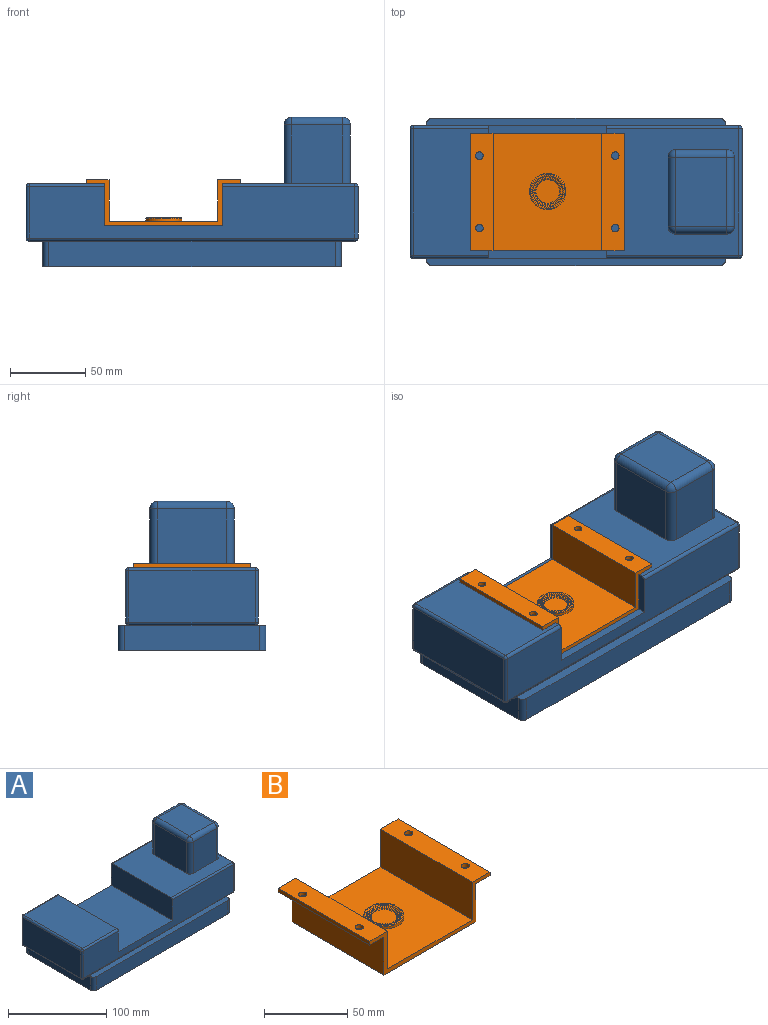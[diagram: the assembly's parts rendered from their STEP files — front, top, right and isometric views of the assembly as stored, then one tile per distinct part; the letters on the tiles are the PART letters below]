
ASSEMBLY  parts=2 mates=1
PART A: 61 faces, bbox 220x98x99 mm
  f0: plane 198x7mm, normal (0,0,1), area 1379.1mm2, adj f2,f3,f4,f7,f8,f37
  f1: plane 198x7mm, normal (0,0,1), area 1379.1mm2, adj f2,f4,f5,f9,f10,f29
  f2: plane 90x17mm, normal (-1,0,0), area 1530mm2, adj f0,f1,f6,f7,f10,f11
  f3: plane 190x17mm, normal (0,-1,0), area 3230mm2, adj f0,f6,f7,f8
  f4: plane 90x17mm, normal (1,0,0), area 1530mm2, adj f0,f1,f6,f8,f9,f18
  f5: plane 190x17mm, normal (0,1,0), area 3230mm2, adj f1,f6,f9,f10
  f6: plane 198x98mm, normal (0,0,-1), area 19390.3mm2, adj f2,f3,f4,f5,f7,f8,f9,f10
  f7: cylinder r=4mm len=17mm, axis (0,0,-1), area 106.8mm2, adj f0,f2,f3,f6
  f8: cylinder r=4mm len=17mm, axis (0,0,1), area 106.8mm2, adj f0,f3,f4,f6
  f9: cylinder r=4mm len=17mm, axis (0,0,-1), area 106.8mm2, adj f1,f4,f5,f6
  f10: cylinder r=4mm len=17mm, axis (0,0,1), area 106.8mm2, adj f1,f2,f5,f6
  f11: plane 84x9mm, normal (0,0,-1), area 756mm2, adj f2,f29,f30,f37
  f12: plane 88x84mm, normal (0,0,1), area 4949.5mm2, adj f19,f34,f40,f43,f44,f45,f46,f47
  f13: plane 216x34mm, normal (0,-1,0), area 5316mm2, adj f19,f20,f21,f26,f31,f37,f41,f43
  f14: plane 216x34mm, normal (0,1,0), area 5316mm2, adj f19,f20,f21,f22,f24,f29,f34,f35
  f15: plane 84x34mm, normal (-1,0,0), area 2856mm2, adj f24,f25,f30,f31
  f16: plane 84x34mm, normal (1,0,0), area 2856mm2, adj f35,f36,f40,f41
  f17: plane 84x50mm, normal (0,0,1), area 4200mm2, adj f20,f22,f25,f26
  f18: plane 84x9mm, normal (0,0,-1), area 756mm2, adj f4,f29,f36,f37
  f19: plane 88x28mm, normal (-1,0,0), area 2462.3mm2, adj f12,f13,f14,f21,f34,f43
  f20: plane 88x28mm, normal (1,0,0), area 2462.3mm2, adj f13,f14,f17,f21,f22,f26
  f21: plane 88x78mm, normal (0,0,1), area 6864mm2, adj f13,f14,f19,f20
  f22: cylinder r=2mm len=50mm, axis (1,0,0), area 157.1mm2, adj f14,f17,f20,f23
  f23: sphere r=2mm, area 6.3mm2, adj f22,f24,f25
  f24: cylinder r=2mm len=34mm, axis (0,0,1), area 106.8mm2, adj f14,f15,f23,f27
  f25: cylinder r=2mm len=84mm, axis (0,1,0), area 263.9mm2, adj f15,f17,f23,f28
  f26: cylinder r=2mm len=50mm, axis (-1,0,0), area 157.1mm2, adj f13,f17,f20,f28
  f27: sphere r=2mm, area 6.3mm2, adj f24,f29,f30
  f28: sphere r=2mm, area 6.3mm2, adj f25,f26,f31
  f29: cylinder r=2mm len=216mm, axis (-1,0,0), area 678.6mm2, adj f1,f11,f14,f18,f27,f32
  f30: cylinder r=2mm len=84mm, axis (0,-1,0), area 263.9mm2, adj f11,f15,f27,f33
  f31: cylinder r=2mm len=34mm, axis (0,0,-1), area 106.8mm2, adj f13,f15,f28,f33
  f32: sphere r=2mm, area 6.3mm2, adj f29,f35,f36
  f33: sphere r=2mm, area 6.3mm2, adj f30,f31,f37
  f34: cylinder r=2mm len=88mm, axis (1,0,0), area 276.5mm2, adj f12,f14,f19,f38
  f35: cylinder r=2mm len=34mm, axis (0,0,-1), area 106.8mm2, adj f14,f16,f32,f38
  f36: cylinder r=2mm len=84mm, axis (0,1,0), area 263.9mm2, adj f16,f18,f32,f39
  f37: cylinder r=2mm len=216mm, axis (1,0,0), area 678.6mm2, adj f0,f11,f13,f18,f33,f39
  f38: sphere r=2mm, area 6.3mm2, adj f34,f35,f40
  f39: sphere r=2mm, area 6.3mm2, adj f36,f37,f41
  f40: cylinder r=2mm len=84mm, axis (0,-1,0), area 263.9mm2, adj f12,f16,f38,f42
  f41: cylinder r=2mm len=34mm, axis (0,0,1), area 106.8mm2, adj f13,f16,f39,f42
  f42: sphere r=2mm, area 6.3mm2, adj f40,f41,f43
  f43: cylinder r=2mm len=88mm, axis (-1,0,0), area 276.5mm2, adj f12,f13,f19,f42
  f44: plane 39x34mm, normal (0,-1,0), area 1326mm2, adj f12,f51,f57,f60
  f45: plane 46x39mm, normal (1,0,0), area 1794mm2, adj f12,f54,f58,f60
  f46: plane 39x34mm, normal (0,1,0), area 1326mm2, adj f12,f49,f53,f54
  f47: plane 46x39mm, normal (-1,0,0), area 1794mm2, adj f12,f49,f51,f52
  f48: plane 46x34mm, normal (0,0,1), area 1564mm2, adj f52,f53,f57,f58
  f49: cylinder r=5mm len=39mm, axis (0,0,-1), area 306.3mm2, adj f12,f46,f47,f50
  f50: sphere r=5mm, area 39.3mm2, adj f49,f52,f53
  f51: cylinder r=5mm len=39mm, axis (0,0,1), area 306.3mm2, adj f12,f44,f47,f55
  f52: cylinder r=5mm len=46mm, axis (0,1,0), area 361.3mm2, adj f47,f48,f50,f55
  f53: cylinder r=5mm len=34mm, axis (1,0,0), area 267mm2, adj f46,f48,f50,f56
  f54: cylinder r=5mm len=39mm, axis (0,0,1), area 306.3mm2, adj f12,f45,f46,f56
  f55: sphere r=5mm, area 39.3mm2, adj f51,f52,f57
  f56: sphere r=5mm, area 39.3mm2, adj f53,f54,f58
  f57: cylinder r=5mm len=34mm, axis (-1,0,0), area 267mm2, adj f44,f48,f55,f59
  f58: cylinder r=5mm len=46mm, axis (0,-1,0), area 361.3mm2, adj f45,f48,f56,f59
  f59: sphere r=5mm, area 39.3mm2, adj f57,f58,f60
  f60: cylinder r=5mm len=39mm, axis (0,0,-1), area 306.3mm2, adj f12,f44,f45,f59
PART B: 27 faces, bbox 102x78x30.7 mm
  f0: plane 78x27.75mm, normal (-1,0,0), area 2164.4mm2, adj f1,f11,f12,f13
  f1: plane 78x72mm, normal (0,0,1), area 5162.1mm2, adj f0,f2,f12,f13,f18
  f2: plane 78x27.75mm, normal (1,0,0), area 2164.4mm2, adj f1,f3,f12,f13
  f3: plane 78x15mm, normal (0,0,1), area 1130.7mm2, adj f2,f4,f12,f13,f16,f17
  f4: plane 78x2.75mm, normal (-1,0,0), area 214.4mm2, adj f3,f5,f12,f13
  f5: plane 78x12mm, normal (0,0,-1), area 896.6mm2, adj f4,f6,f12,f13,f16,f17
  f6: plane 78x28mm, normal (-1,0,0), area 2184mm2, adj f5,f7,f12,f13
  f7: plane 78x78mm, normal (0,0,-1), area 6084mm2, adj f6,f8,f12,f13
  f8: plane 78x28mm, normal (1,0,0), area 2184mm2, adj f7,f9,f12,f13
  f9: plane 78x12mm, normal (0,0,-1), area 896.6mm2, adj f8,f10,f12,f13,f14,f15
  f10: plane 78x2.75mm, normal (1,0,0), area 214.4mm2, adj f9,f11,f12,f13
  f11: plane 78x15mm, normal (0,0,1), area 1130.7mm2, adj f0,f10,f12,f13,f14,f15
  f12: plane 102x30.75mm, normal (0,-1,0), area 466.5mm2, adj f0,f1,f2,f3,f4,f5,f6,f7
  f13: plane 102x30.75mm, normal (0,1,0), area 466.5mm2, adj f0,f1,f2,f3,f4,f5,f6,f7
  f14: cylinder r=2.5mm len=5mm, axis (0,0,1), area 43.2mm2, adj f9,f11
  f15: cylinder r=2.5mm len=5mm, axis (0,0,1), area 43.2mm2, adj f9,f11
  f16: cylinder r=2.5mm len=5mm, axis (0,0,1), area 43.2mm2, adj f3,f5
  f17: cylinder r=2.5mm len=5mm, axis (0,0,1), area 43.2mm2, adj f3,f5
  f18: cylinder r=12.02mm len=24.04mm, axis (0,0,-1), area 135.9mm2, adj f1,f26
  f19: plane 23.04x23.04mm, normal (0,0,1), area 63.8mm2, adj f25,f26
  f20: plane 19.2x19.2mm, normal (0,0,1), area 47.8mm2, adj f23,f24
  f21: plane 15.55x15.55mm, normal (0,0,1), area 189.8mm2, adj f22
  f22: torus R=7.77mm, axis (0,0,1), area 39.9mm2, adj f21,f23
  f23: torus R=8.77mm, axis (0,0,1), area 41.7mm2, adj f20,f22
  f24: torus R=9.6mm, axis (0,0,1), area 48.9mm2, adj f20,f25
  f25: torus R=10.6mm, axis (0,0,-1), area 50.7mm2, adj f19,f24
  f26: torus R=11.52mm, axis (0,0,-1), area 58.4mm2, adj f18,f19
PLACE A t=(0,0,0.25)mm
PLACE B t=(-6.02,-4.81,36.88)mm
MATE fastened B.f7 <-> A.f21  axis (0,0,1) through (-8.99,-4.81,27.25)mm
